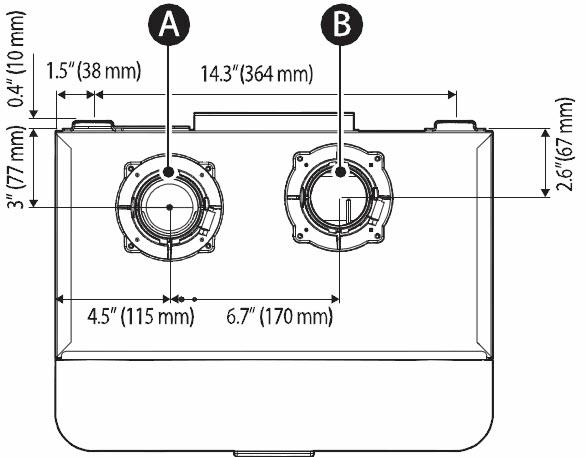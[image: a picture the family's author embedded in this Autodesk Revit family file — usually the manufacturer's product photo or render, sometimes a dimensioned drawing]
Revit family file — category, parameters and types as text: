
# Revit family: Water_Heater-Racks-Navien-NPE-16_Unit_Front-Wall-02
name_source: partatom
category: Mechanical Equipment
revit_build: Autodesk Revit 2016 (Build: 20150220_1215(x64)
units: mm (PartAtom-declared; Revit-internal decimal feet)

## family parameters
Cut with Voids When Loaded = No
Host = Face
OmniClass Number = 23.65.35.11
OmniClass Title = Supply Water Heaters
Part Type = Normal
Room Calculation Point = No
Round Connector Dimension = Use Diameter
Shared = No

## types (4) — shared parameters
2" Exhaust/Intake = Yes
3" Exhaust/Intake = No
Apparent Load = 0 VA
Assembly Code = D3010500
Certifications = Energy Star | AHRI | CSA | CSA | NFS
Cold Water Inlet = 1"
Configuration = NPE_F16_4F4F_4F4F
Default Elevation = 48 "
Depth = 23.8 "
Description = 16 Unit Front
Exhaust = 2"
Finish = Metal - Navien - White
Flow Rate = 1 GPM
Flow Rate Note = 35°F (19°C) temp rise: 11.2 GPM (42 L/m) | 45°F (25°C) temp rise: 8.7 GPM (33 L/m) | 67°F (36°C) temp rise: NPE-240A: 5.6 GPM(21 L/m), NPE-240S: 5.7 GPM(22 L/m)
Frequency = 60 Hz
Gas Inlet = 1"
Heating Capacity = 120000.0 Btu/h
Heating Capacity Note = 19,900–199,900 (BTU/H)
Height = 65.5 "
Hot Water Outlet = 1"
Ignition = Electronic ignition
Installation Type = Indoor
Intake = 2"
Keynote = 22 33 00.A1
Manifold(s) = (4) 30019043A
Manufacturer = Navien, Inc.
Manufacturer Fax Number = (949) 420-0430
Natural Gas Manifold Pressure = -0.05" WC to -0.58" WC
Natural Gas Supply Pressure = 3.5"–10.5" WC
Number of Poles = 1
Phase = 1
Power Factor = 1
Product Documentation Link = https://www.navieninc.com
Product Name = NPE Series Tankless Water Heaters w/ Racks
Product Page URL = https://www.navieninc.com
Propane Gas Manifold Pressure = -0.10" WC to -0.78" WC
Propane Gas Supply Pressure = 8"–13" WC
Required Cascade Operation Accessory = (16) 30014367A (Common Vent Damper & Cascade Communication Cable) or (1) GXXX000546 (Individual Vent Cascade Communication Cable)
URL = https://www.navieninc.com
Venting = Exhaust: 2" PVC, CPVC, PP, SS / 2" special gas vent type BH (Class II, A/B/C) | Intake: 2" PVC, CPVC, PP, SS / 2" special gas vent type BH (Class II, A/B/C) | Vent clearances: 0" to combustibles
Venting Type = Forced draft direct vent
Version = 2016 - v1.0.a
Voltage = 120 V
Water Pressure = 15–150 PSI
Wi-Fi Ready = NaviLink Wi-Fi Control: PBCM-AS-001
Width = 342.3 "

## per-type parameters (varying)
| type | Constraints | Model | Natural Gas | Propane Gas | Recirculation Inlet | Recirculation Inlet Visibility | Tankless Water Heaters | Weight |
| Natural Gas - Recirculating System - NPE-240A(Advanced)-NG | 6 | (16) NPE-240A-NG | Yes | No | 0" | Yes | (16) NPE-240A-NG | 82.00 lbf |
| Natural Gas - NPE-240S(Standard)-NG | 7 | (16) NPE-240S-NG | Yes | No | 1" | No | (16) NPE-240S-NG | 75.00 lbf |
| Propane Gas - Recirculating System - NPE-240A(Advanced)-LPG | 6 | (16) NPE-240A-LPG | No | Yes | 0" | Yes | (16) NPE-240A-LPG | 82.00 lbf |
| Propane Gas - NPE-240S(Standard)-LPG | 7 | (16) NPE-240S-LPG | No | Yes | 1" | No | (16) NPE-240S-LPG | 75.00 lbf |

## geometry (parser evidence)
native form markers: Sweep x9
no freeform markers — native parametric forms only
